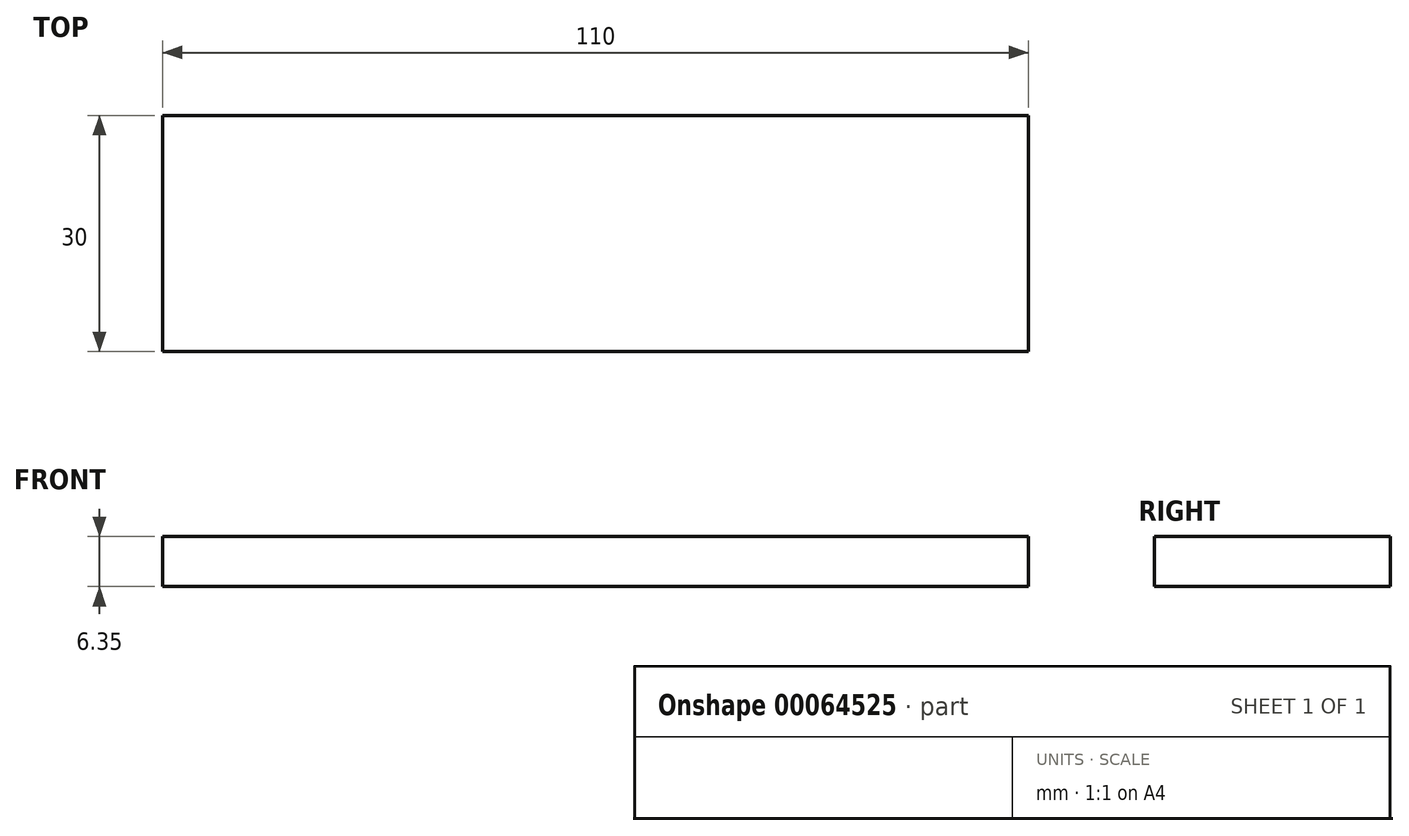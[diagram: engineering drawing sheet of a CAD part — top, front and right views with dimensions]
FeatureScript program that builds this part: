
annotation { "Feature Type Name" : "Feature", "Feature Type Description" : "" }
export const myFeature = defineFeature(function(context is Context, id is Id, definition is map)
    precondition{}
    {
        {
            var Q0;
            Q0=qCreatedBy(makeId("Top.planeOp"),FACE);
            var sketch = newSketch(context, id + "F0", { "sketchPlane" : qUnion([Q0])});
            skLineSegment(sketch, "E0.bottom", {"start": v(-33.55, 19.97) * mm, "end": v(76.45, 19.97) * mm});
            skLineSegment(sketch, "E0.top", {"start": v(-33.55, -10.03) * mm, "end": v(76.45, -10.03) * mm});
            skLineSegment(sketch, "E0.left", {"start": v(-33.55, 19.97) * mm, "end": v(-33.55, -10.03) * mm});
            skLineSegment(sketch, "E0.right", {"start": v(76.45, 19.97) * mm, "end": v(76.45, -10.03) * mm});
            skSolve(sketch);
        }
        {
            var Q0;
            Q0=makeQuery(id+"F0.imprint","IMPRINT",FACE,{"disambiguationData":[TD([[makeQuery(id+"F0.imprint","IMPRINT",EDGE,{"derivedFrom":sQuery(id+"F0.wireOp",EDGE,"E0.bottom")}),-1.0]])]});
            extrude(context, id + "F1", {"entities" : qUnion([Q0]), "depth" : 6.35 * mm});
        }
    });
